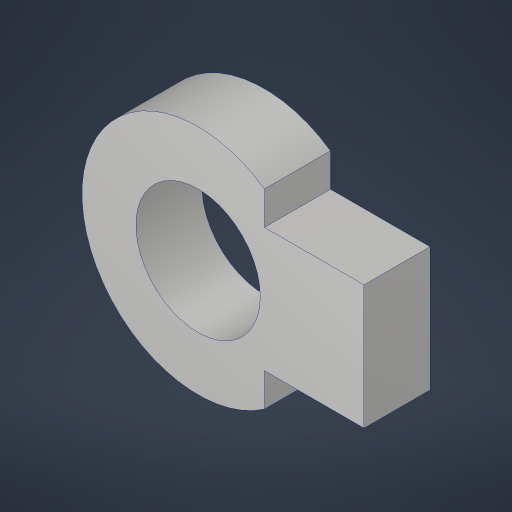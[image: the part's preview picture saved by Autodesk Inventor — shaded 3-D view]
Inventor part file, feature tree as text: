
AUTODESK INVENTOR PART (.ipt)
format: ipt  version: 2023.4 (Build 274418000, 418)  size: 173,568 bytes
history: native  units: in
note: dims shown in document units (in); Inventor stores cm internally (conversion verified against a paired STEP export)
features: extrude x1, sketch x1
ambient origin geometry x8: Origin, YZ Plane, XZ Plane, XY Plane, X Axis, Y Axis, Z Axis, Center Point
bodies: Solid1 (feature_tree)
feature tree (2):
  extrude  "Extrusion1"  Depth=0.995in
  sketch  "Sketch1"  dims[d0=1.875in d1=3.5in d2=1.87in d3=1.5in d4=1.0in d5=0.995in d6=0.0in]
